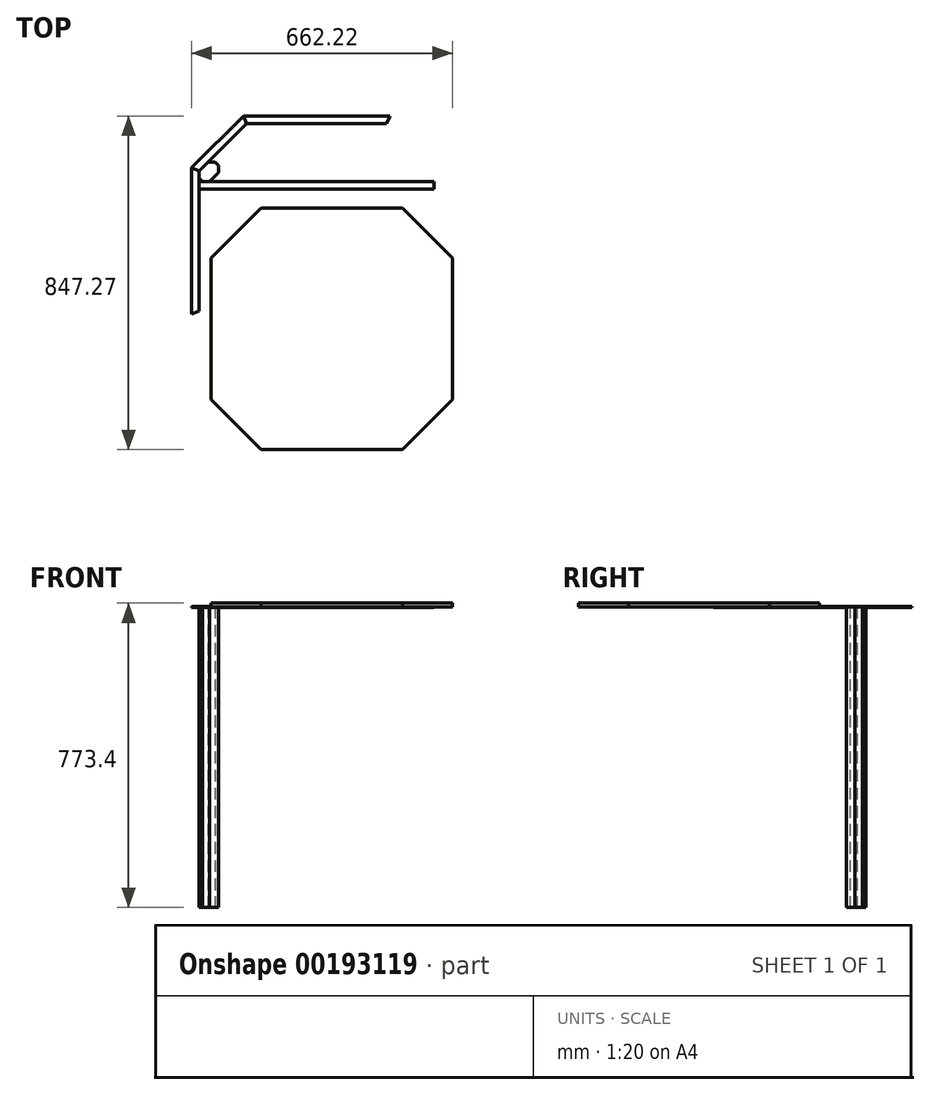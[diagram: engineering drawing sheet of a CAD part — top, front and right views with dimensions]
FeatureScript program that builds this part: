
annotation { "Feature Type Name" : "Feature", "Feature Type Description" : "" }
export const myFeature = defineFeature(function(context is Context, id is Id, definition is map)
    precondition{}
    {
        {
            assignVariable(context, id + "F0", {"name" : "topdepth", "anyValue" : 2.5});
        }
        {
            var Q0;
            Q0=qCreatedBy(makeId("Top.planeOp"),FACE);
            var sketch = newSketch(context, id + "F1", { "sketchPlane" : qUnion([Q0])});
            skLineSegment(sketch, "E0", {"start": v(0, 0) * mm, "end": v(19.05, 7.9) * mm});
            skLineSegment(sketch, "E1", {"start": v(19.05, 7.9) * mm, "end": v(19.05, 363.97) * mm});
            skLineSegment(sketch, "E2", {"start": v(19.05, 363.97) * mm, "end": v(0, 371.86) * mm});
            skLineSegment(sketch, "E3", {"start": v(0, 371.86) * mm, "end": v(0, 0) * mm});
            skLineSegment(sketch, "E4", {"start": v(0, 371.86) * mm, "end": v(131.47, 503.33) * mm});
            skLineSegment(sketch, "E5", {"start": v(131.47, 503.33) * mm, "end": v(139.36, 484.28) * mm});
            skLineSegment(sketch, "E6", {"start": v(139.36, 484.28) * mm, "end": v(19.05, 363.97) * mm});
            skLineSegment(sketch, "E7", {"start": v(131.47, 503.33) * mm, "end": v(503.33, 503.33) * mm});
            skLineSegment(sketch, "E8", {"start": v(503.33, 503.33) * mm, "end": v(495.44, 484.28) * mm});
            skLineSegment(sketch, "E9", {"start": v(495.44, 484.28) * mm, "end": v(139.36, 484.28) * mm});
            skLineSegment(sketch, "E10.0", {"start": v(46, 337.02) * mm, "end": v(28.03, 337.02) * mm});
            skLineSegment(sketch, "E10.1", {"start": v(28.03, 337.02) * mm, "end": v(19.05, 346) * mm});
            skLineSegment(sketch, "E10.2", {"start": v(19.05, 346) * mm, "end": v(19.05, 363.97) * mm});
            skLineSegment(sketch, "E10.3", {"start": v(19.05, 363.97) * mm, "end": v(41.5, 386.42) * mm});
            skLineSegment(sketch, "E10.4", {"start": v(41.5, 386.42) * mm, "end": v(59.46, 386.42) * mm});
            skLineSegment(sketch, "E10.5", {"start": v(59.46, 386.42) * mm, "end": v(68.44, 377.44) * mm});
            skLineSegment(sketch, "E10.6", {"start": v(68.44, 377.44) * mm, "end": v(68.44, 359.48) * mm});
            skLineSegment(sketch, "E10.7", {"start": v(68.44, 359.48) * mm, "end": v(46, 337.02) * mm});
            skPoint(sketch, "E10.0.midPoint", {"position": v(28.03, 337.02) * mm});
            skLineSegment(sketch, "E11.bottom", {"start": v(19.05, 337.02) * mm, "end": v(615.75, 337.02) * mm});
            skLineSegment(sketch, "E11.top", {"start": v(19.05, 317.97) * mm, "end": v(615.75, 317.97) * mm});
            skLineSegment(sketch, "E11.left", {"start": v(19.05, 337.02) * mm, "end": v(19.05, 317.97) * mm});
            skLineSegment(sketch, "E11.right", {"start": v(615.75, 337.02) * mm, "end": v(615.75, 317.97) * mm});
            skSolve(sketch);
        }
        {
            var Q0;
            Q0=makeQuery(id+"F1.imprint","IMPRINT",FACE,{"disambiguationData":[TD([[makeQuery(id+"F1.imprint","IMPRINT",EDGE,{"derivedFrom":sQuery(id+"F1.wireOp",EDGE,"E0")}),1.0]])]});
            extrude(context, id + "F2", {"entities" : qUnion([Q0]), "depth" : (getVariable(context, 'topdepth')) * mm});
        }
        {
            var Q0;
            Q0=makeQuery(id+"F1.imprint","IMPRINT",FACE,{"disambiguationData":[TD([[makeQuery(id+"F1.imprint","IMPRINT",EDGE,{"derivedFrom":sQuery(id+"F1.wireOp",EDGE,"E2")}),-1.0]])]});
            extrude(context, id + "F3", {"entities" : qUnion([Q0]), "depth" : (getVariable(context, 'topdepth')) * mm});
        }
        {
            var Q0;
            Q0=makeQuery(id+"F1.imprint","IMPRINT",FACE,{"disambiguationData":[TD([[makeQuery(id+"F1.imprint","IMPRINT",EDGE,{"derivedFrom":sQuery(id+"F1.wireOp",EDGE,"E5")}),1.0]])]});
            extrude(context, id + "F4", {"entities" : qUnion([Q0]), "depth" : (getVariable(context, 'topdepth')) * mm});
        }
        {
            var Q0;
            {var subQ1=sQuery(id+"F1.wireOp",EDGE,"E10.1");Q0=makeQuery(id+"F1.imprint","IMPRINT",FACE,{"disambiguationData":[TD([[makeQuery(id+"F1.imprint","IMPRINT",EDGE,{"derivedFrom":subQ1}),-1.0]])]});}
            extrude(context, id + "F5", {"entities" : qUnion([Q0]), "depth" : (getVariable(context, 'topdepth') - .25 - .375) * mm, "hasSecondDirection" : true, "secondDirectionOppositeDirection" : true, "secondDirectionDepth" : 762 * mm});
        }
        {
            var Q0;
            Q0=makeQuery(id+"F1.imprint","IMPRINT",FACE,{"disambiguationData":[TD([[makeQuery(id+"F1.imprint","IMPRINT",EDGE,{"derivedFrom":sQuery(id+"F1.wireOp",EDGE,"E11.top")}),1.0]])]});
            extrude(context, id + "F6", {"entities" : qUnion([Q0]), "depth" : (getVariable(context, 'topdepth') - .25 - .375) * mm});
        }
        {
            var Q0;
            Q0=makeQuery(id+"F2.opExtrude","SWEPT_FACE",FACE,{"disambiguationData":[OSD([sQuery(id+"F1.wireOp",EDGE,"E1"),sQuery(id+"F1.wireOp",EDGE,"E10.2"),sQuery(id+"F1.wireOp",EDGE,"E11.left")])]});
            var sketch = newSketch(context, id + "F7", { "sketchPlane" : qUnion([Q0])});
            skLineSegment(sketch, "E12.bottom", {"start": v(0, 57.15) * mm, "end": v(371.86, 57.15) * mm});
            skLineSegment(sketch, "E12.top", {"start": v(0, 47.63) * mm, "end": v(371.86, 47.63) * mm});
            skLineSegment(sketch, "E12.left", {"start": v(0, 57.15) * mm, "end": v(0, 47.63) * mm});
            skLineSegment(sketch, "E12.right", {"start": v(371.86, 57.15) * mm, "end": v(371.86, 47.63) * mm});
            skSolve(sketch);
        }
        {
            var Q0;
            {var subQ0=sQuery(id+"F7.wireOp",EDGE,"E12.bottom");var subQ1=makeQuery(id+"F2.opExtrude","SWEPT_EDGE",EDGE,{"disambiguationData":[OSD([sQuery(id+"F1.wireOp",EDGE,"E0"),sQuery(id+"F1.wireOp",EDGE,"E1")])]});var subQ2=makeQuery(id+"F7.imprint","INTERSECT",VERTEX,{"derivedFrom":[subQ1,subQ0]});Q0=makeQuery(id+"F7.imprint","IMPRINT",FACE,{"disambiguationData":[TD([[makeQuery(id+"F7.imprint","IMPRINT",EDGE,{"disambiguationData":[TD([[subQ2,-1.0]])],"derivedFrom":subQ0}),-1.0]])]});}
            var Q1;
            {var subQ0=sQuery(id+"F7.wireOp",EDGE,"E12.right");Q1=makeQuery(id+"F7.imprint","IMPRINT",FACE,{"disambiguationData":[TD([[makeQuery(id+"F7.imprint","IMPRINT",EDGE,{"derivedFrom":subQ0}),-1.0]])]});}
            var Q2;
            {var subQ0=sQuery(id+"F7.wireOp",EDGE,"E12.left");Q2=makeQuery(id+"F7.imprint","IMPRINT",FACE,{"disambiguationData":[TD([[makeQuery(id+"F7.imprint","IMPRINT",EDGE,{"derivedFrom":subQ0}),1.0]])]});}
            extrude(context, id + "F8", {"entities" : qUnion([Q0, Q1, Q2]), "operationType" : NewBodyOperationType.REMOVE, "oppositeDirection" : true, "depth" : 6.35 * mm});
        }
        {
            var Q0;
            Q0=makeQuery(id+"F3.opExtrude","SWEPT_FACE",FACE,{"disambiguationData":[OSD([sQuery(id+"F1.wireOp",EDGE,"E6"),sQuery(id+"F1.wireOp",EDGE,"E10.3")])]});
            var sketch = newSketch(context, id + "F9", { "sketchPlane" : qUnion([Q0])});
            skLineSegment(sketch, "E13.bottom", {"start": v(262.94, 57.15) * mm, "end": v(448.87, 57.15) * mm});
            skLineSegment(sketch, "E13.top", {"start": v(262.94, 47.63) * mm, "end": v(448.87, 47.63) * mm});
            skLineSegment(sketch, "E13.left", {"start": v(262.94, 57.15) * mm, "end": v(262.94, 47.63) * mm});
            skLineSegment(sketch, "E13.right", {"start": v(448.87, 57.15) * mm, "end": v(448.87, 47.63) * mm});
            skSolve(sketch);
        }
        {
            var Q0;
            {var subQ0=sQuery(id+"F9.wireOp",EDGE,"E13.left");Q0=makeQuery(id+"F9.imprint","IMPRINT",FACE,{"disambiguationData":[TD([[makeQuery(id+"F9.imprint","IMPRINT",EDGE,{"derivedFrom":subQ0}),1.0]])]});}
            var Q1;
            {var subQ0=sQuery(id+"F9.wireOp",EDGE,"E13.bottom");var subQ1=makeQuery(id+"F3.opExtrude","SWEPT_EDGE",EDGE,{"disambiguationData":[OSD([sQuery(id+"F1.wireOp",EDGE,"E2"),sQuery(id+"F1.wireOp",EDGE,"E10.2"),sQuery(id+"F1.wireOp",EDGE,"E10.3")])]});var subQ2=makeQuery(id+"F9.imprint","INTERSECT",VERTEX,{"derivedFrom":[subQ1,subQ0]});Q1=makeQuery(id+"F9.imprint","IMPRINT",FACE,{"disambiguationData":[TD([[makeQuery(id+"F9.imprint","IMPRINT",EDGE,{"disambiguationData":[TD([[subQ2,-1.0]])],"derivedFrom":subQ0}),-1.0]])]});}
            var Q2;
            {var subQ0=sQuery(id+"F9.wireOp",EDGE,"E13.right");Q2=makeQuery(id+"F9.imprint","IMPRINT",FACE,{"disambiguationData":[TD([[makeQuery(id+"F9.imprint","IMPRINT",EDGE,{"derivedFrom":subQ0}),-1.0]])]});}
            extrude(context, id + "F10", {"entities" : qUnion([Q0, Q1, Q2]), "operationType" : NewBodyOperationType.REMOVE, "oppositeDirection" : true, "depth" : 6.35 * mm});
        }
        {
            var Q0;
            Q0=makeQuery(id+"F4.opExtrude","SWEPT_FACE",FACE,{"disambiguationData":[OSD([sQuery(id+"F1.wireOp",EDGE,"E9")])]});
            var sketch = newSketch(context, id + "F11", { "sketchPlane" : qUnion([Q0])});
            skLineSegment(sketch, "E14.bottom", {"start": v(131.47, 57.15) * mm, "end": v(503.33, 57.15) * mm});
            skLineSegment(sketch, "E14.top", {"start": v(131.47, 47.63) * mm, "end": v(503.33, 47.63) * mm});
            skLineSegment(sketch, "E14.left", {"start": v(131.47, 57.15) * mm, "end": v(131.47, 47.63) * mm});
            skLineSegment(sketch, "E14.right", {"start": v(503.33, 57.15) * mm, "end": v(503.33, 47.63) * mm});
            skSolve(sketch);
        }
        {
            var Q0;
            {var subQ0=sQuery(id+"F11.wireOp",EDGE,"E14.left");Q0=makeQuery(id+"F11.imprint","IMPRINT",FACE,{"disambiguationData":[TD([[makeQuery(id+"F11.imprint","IMPRINT",EDGE,{"derivedFrom":subQ0}),1.0]])]});}
            var Q1;
            {var subQ0=sQuery(id+"F11.wireOp",EDGE,"E14.bottom");var subQ1=sQuery(id+"F1.wireOp",EDGE,"E9");var subQ4=makeQuery(id+"F4.opExtrude","SWEPT_EDGE",EDGE,{"disambiguationData":[OSD([sQuery(id+"F1.wireOp",EDGE,"E8"),subQ1])]});var subQ5=makeQuery(id+"F11.imprint","INTERSECT",VERTEX,{"derivedFrom":[subQ4,subQ0]});Q1=makeQuery(id+"F11.imprint","IMPRINT",FACE,{"disambiguationData":[TD([[makeQuery(id+"F11.imprint","IMPRINT",EDGE,{"disambiguationData":[TD([[subQ5,1.0]])],"derivedFrom":subQ0}),-1.0]])]});}
            var Q2;
            {var subQ0=sQuery(id+"F11.wireOp",EDGE,"E14.right");Q2=makeQuery(id+"F11.imprint","IMPRINT",FACE,{"disambiguationData":[TD([[makeQuery(id+"F11.imprint","IMPRINT",EDGE,{"derivedFrom":subQ0}),-1.0]])]});}
            extrude(context, id + "F12", {"entities" : qUnion([Q0, Q1, Q2]), "operationType" : NewBodyOperationType.REMOVE, "oppositeDirection" : true, "depth" : 6.35 * mm});
        }
        {
            var Q0;
            Q0=makeQuery(id+"F6.opExtrude","CAP_FACE",FACE,{"disambiguationData":[OSD([sQuery(id+"F1.wireOp",EDGE,"E11.bottom"),sQuery(id+"F1.wireOp",EDGE,"E11.top"),sQuery(id+"F1.wireOp",EDGE,"E11.left"),sQuery(id+"F1.wireOp",EDGE,"E11.right")])],"isStart":false});
            var sketch = newSketch(context, id + "F13", { "sketchPlane" : qUnion([Q0])});
            skLineSegment(sketch, "E15", {"start": v(49.1, -216.95) * mm, "end": v(49.1, 142.2) * mm});
            skLineSegment(sketch, "E16", {"start": v(49.1, 142.2) * mm, "end": v(176.08, 269.18) * mm});
            skLineSegment(sketch, "E17", {"start": v(176.08, 269.18) * mm, "end": v(535.24, 269.18) * mm});
            skLineSegment(sketch, "E18", {"start": v(535.24, 269.18) * mm, "end": v(662.22, 142.2) * mm});
            skLineSegment(sketch, "E19", {"start": v(662.22, 142.2) * mm, "end": v(662.22, -216.95) * mm});
            skLineSegment(sketch, "E20", {"start": v(662.22, -216.95) * mm, "end": v(535.24, -343.94) * mm});
            skLineSegment(sketch, "E21", {"start": v(535.24, -343.94) * mm, "end": v(176.08, -343.94) * mm});
            skLineSegment(sketch, "E22", {"start": v(176.08, -343.94) * mm, "end": v(49.1, -216.95) * mm});
            skSolve(sketch);
        }
        {
            var Q0;
            Q0=makeQuery(id+"F13.imprint","IMPRINT",FACE,{"disambiguationData":[TD([[makeQuery(id+"F13.imprint","IMPRINT",EDGE,{"derivedFrom":sQuery(id+"F13.wireOp",EDGE,"E15")}),-1.0]])]});
            extrude(context, id + "F14", {"entities" : qUnion([Q0]), "depth" : 9.52 * mm});
        }
    });
